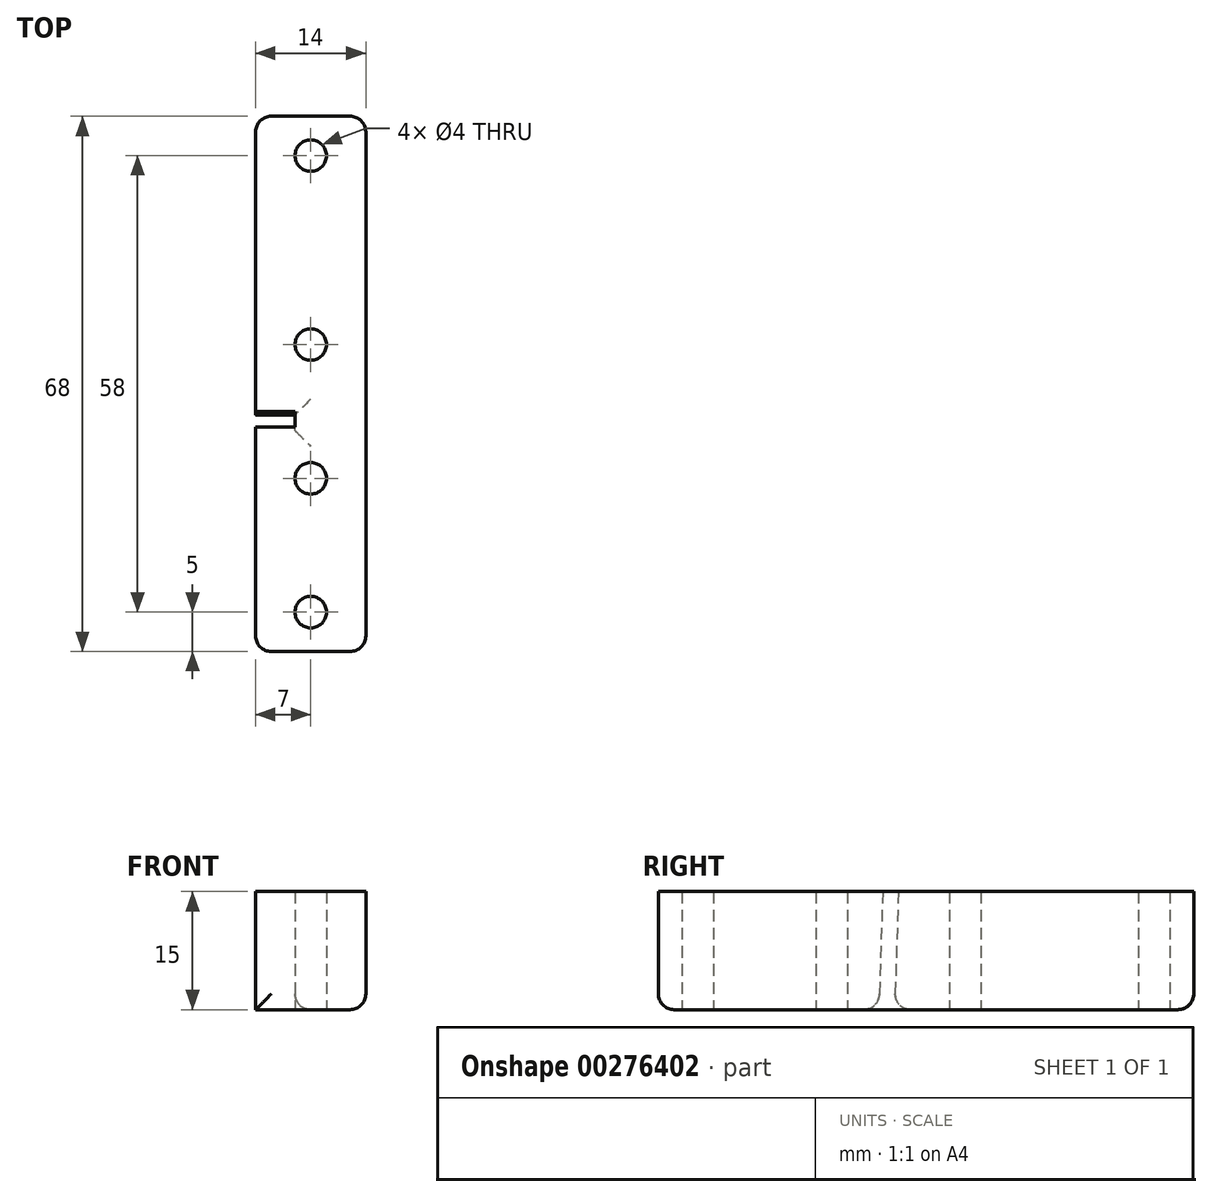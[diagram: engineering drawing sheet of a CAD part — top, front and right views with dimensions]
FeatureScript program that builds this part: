
annotation { "Feature Type Name" : "Feature", "Feature Type Description" : "" }
export const myFeature = defineFeature(function(context is Context, id is Id, definition is map)
    precondition{}
    {
        {
            var Q0;
            Q0=qCreatedBy(makeId("Top.planeOp"),FACE);
            var sketch = newSketch(context, id + "F0", { "sketchPlane" : qUnion([Q0])});
            skLineSegment(sketch, "E0.bottom", {"start": v(0, 0) * mm, "end": v(14, 0) * mm});
            skLineSegment(sketch, "E0.top", {"start": v(0, 68) * mm, "end": v(14, 68) * mm});
            skLineSegment(sketch, "E0.left", {"start": v(0, 0) * mm, "end": v(0, 28) * mm});
            skLineSegment(sketch, "E0.right", {"start": v(14, 0) * mm, "end": v(14, 28) * mm});
            skCircle(sketch, "E1", {"center": v(7, 5) * mm, "radius": 2 * mm});
            skPoint(sketch, "E1.centerSnap0", {"position": v(7, 0) * mm});
            skCircle(sketch, "E2", {"center": v(7, 22) * mm, "radius": 2 * mm});
            skLineSegment(sketch, "E3.bottom", {"start": v(0, 30) * mm, "end": v(14, 30) * mm});
            skLineSegment(sketch, "E3.top", {"start": v(0, 28) * mm, "end": v(14, 28) * mm});
            skLineSegment(sketch, "E4.trimOffspring", {"start": v(0, 30) * mm, "end": v(0, 68) * mm});
            skCircle(sketch, "E5", {"center": v(7, 39) * mm, "radius": 2 * mm});
            skLineSegment(sketch, "E6.trimOffspring", {"start": v(14, 30) * mm, "end": v(14, 68) * mm});
            skCircle(sketch, "E7", {"center": v(7, 63) * mm, "radius": 2 * mm});
            skSolve(sketch);
        }
        {
            var Q0;
            Q0=qSketchRegion(id+"F0",true);
            extrude(context, id + "F1", {"entities" : qUnion([Q0]), "offsetDistance" : 25 * mm, "depth" : 15 * mm});
        }
        {
            var Q0;
            Q0=makeQuery(id+"F1.opExtrude","SWEPT_FACE",FACE,{"disambiguationData":[OSD([sQuery(id+"F0.wireOp",EDGE,"E0.right")])]});
            var sketch = newSketch(context, id + "F2", { "sketchPlane" : qUnion([Q0])});
            skLineSegment(sketch, "E8.bottom", {"start": v(28, 15) * mm, "end": v(30.63, 15) * mm});
            skLineSegment(sketch, "E8.top", {"start": v(28, 0) * mm, "end": v(30.63, 0) * mm});
            skLineSegment(sketch, "E8.left", {"start": v(28, 15) * mm, "end": v(28, 0) * mm});
            skLineSegment(sketch, "E8.right", {"start": v(30.63, 15) * mm, "end": v(30.63, 0) * mm});
            skSolve(sketch);
        }
        {
            var Q0;
            Q0 = qSketchRegion(id + "F2", true);
            extrude(context, id + "F3", {"entities" : qUnion([Q0]), "operationType" : NewBodyOperationType.ADD, "oppositeDirection" : true, "depth" : 9 * mm, "offsetDistance" : 25 * mm});
        }
        {
            var Q0;
            Q0=makeQuery(id+"F1.opExtrude","SWEPT_FACE",FACE,{"disambiguationData":[OSD([sQuery(id+"F0.wireOp",EDGE,"E0.left")])]});
            var sketch = newSketch(context, id + "F4", { "sketchPlane" : qUnion([Q0])});
            skLineSegment(sketch, "E9", {"start": v(-28, 15) * mm, "end": v(-28.5, 15) * mm});
            skLineSegment(sketch, "E10", {"start": v(-28.5, 15) * mm, "end": v(-28, 0) * mm});
            skLineSegment(sketch, "E11", {"start": v(-28, 0) * mm, "end": v(-28, 15) * mm});
            skSolve(sketch);
        }
        {
            var Q0;
            Q0 = qSketchRegion(id + "F4", true);
            extrude(context, id + "F5", {"entities" : qUnion([Q0]), "operationType" : NewBodyOperationType.ADD, "oppositeDirection" : true, "depth" : 5 * mm, "offsetDistance" : 25 * mm});
        }
        {
            var Q0;
            Q0=makeQuery(id+"F1.opExtrude","SWEPT_FACE",FACE,{"disambiguationData":[OSD([sQuery(id+"F0.wireOp",EDGE,"E4.trimOffspring")])]});
            var sketch = newSketch(context, id + "F6", { "sketchPlane" : qUnion([Q0])});
            skLineSegment(sketch, "E12", {"start": v(-30, 15) * mm, "end": v(-30.5, 15) * mm});
            skLineSegment(sketch, "E13", {"start": v(-30.5, 15) * mm, "end": v(-30, 0) * mm});
            skLineSegment(sketch, "E14", {"start": v(-30, 0) * mm, "end": v(-30, 15) * mm});
            skSolve(sketch);
        }
        {
            var Q0;
            Q0 = qSketchRegion(id + "F6", true);
            extrude(context, id + "F7", {"entities" : qUnion([Q0]), "operationType" : NewBodyOperationType.REMOVE, "oppositeDirection" : true, "depth" : 5 * mm, "offsetDistance" : 25 * mm});
        }
        {
            var Q0;
            Q0=makeQuery(id+"F7.boolean.opBoolean","MERGE",EDGE,{"derivedFrom":[makeQuery(id+"F1.opExtrude","CAP_EDGE",EDGE,{"disambiguationData":[OSD([sQuery(id+"F0.wireOp",EDGE,"E3.bottom")])],"isStart":true}),makeQuery(id+"F7.opExtrude","SWEPT_EDGE",EDGE,{"disambiguationData":[OSD([sQuery(id+"F0.wireOp",EDGE,"E4.trimOffspring"),sQuery(id+"F6.wireOp",EDGE,"E13"),sQuery(id+"F6.wireOp",EDGE,"E14")])]})]});
            var Q1;
            Q1=makeQuery(id+"F3.opExtrude","CAP_EDGE",EDGE,{"disambiguationData":[OSD([sQuery(id+"F2.wireOp",EDGE,"E8.top")])],"isStart":false});
            var Q2;
            Q2=makeQuery(id+"F5.boolean.opBoolean","MERGE",EDGE,{"derivedFrom":[makeQuery(id+"F1.opExtrude","CAP_EDGE",EDGE,{"disambiguationData":[OSD([sQuery(id+"F0.wireOp",EDGE,"E3.top")])],"isStart":true}),makeQuery(id+"F5.opExtrude","SWEPT_EDGE",EDGE,{"disambiguationData":[OSD([sQuery(id+"F0.wireOp",EDGE,"E0.left"),sQuery(id+"F4.wireOp",EDGE,"E10"),sQuery(id+"F4.wireOp",EDGE,"E11")])]})]});
            var Q3;
            Q3=makeQuery(id+"F1.opExtrude","CAP_EDGE",EDGE,{"disambiguationData":[OSD([sQuery(id+"F0.wireOp",EDGE,"E0.bottom")])],"isStart":true});
            var Q4;
            Q4=makeQuery(id+"F3.boolean.opBoolean","MERGE",EDGE,{"derivedFrom":[makeQuery(id+"F1.opExtrude","CAP_EDGE",EDGE,{"disambiguationData":[OSD([sQuery(id+"F0.wireOp",EDGE,"E0.right")])],"isStart":true}),makeQuery(id+"F1.opExtrude","CAP_EDGE",EDGE,{"disambiguationData":[OSD([sQuery(id+"F0.wireOp",EDGE,"E6.trimOffspring")])],"isStart":true}),makeQuery(id+"F3.opExtrude","CAP_EDGE",EDGE,{"disambiguationData":[OSD([sQuery(id+"F2.wireOp",EDGE,"E8.top")])],"isStart":true})]});
            var Q5;
            Q5=makeQuery(id+"F1.opExtrude","CAP_EDGE",EDGE,{"disambiguationData":[OSD([sQuery(id+"F0.wireOp",EDGE,"E0.top")])],"isStart":true});
            var Q6;
            Q6=makeQuery(id+"F1.opExtrude","SWEPT_EDGE",EDGE,{"disambiguationData":[OSD([sQuery(id+"F0.wireOp",EDGE,"E0.top"),sQuery(id+"F0.wireOp",EDGE,"E4.trimOffspring")])]});
            var Q7;
            Q7=makeQuery(id+"F1.opExtrude","SWEPT_EDGE",EDGE,{"disambiguationData":[OSD([sQuery(id+"F0.wireOp",EDGE,"E0.top"),sQuery(id+"F0.wireOp",EDGE,"E6.trimOffspring")])]});
            var Q8;
            Q8=makeQuery(id+"F1.opExtrude","SWEPT_EDGE",EDGE,{"disambiguationData":[OSD([sQuery(id+"F0.wireOp",EDGE,"E0.bottom"),sQuery(id+"F0.wireOp",EDGE,"E0.left")])]});
            var Q9;
            Q9=makeQuery(id+"F1.opExtrude","SWEPT_EDGE",EDGE,{"disambiguationData":[OSD([sQuery(id+"F0.wireOp",EDGE,"E0.bottom"),sQuery(id+"F0.wireOp",EDGE,"E0.right")])]});
            fillet(context, id + "F8", {"entities" : qUnion([Q0, Q1, Q2, Q3, Q4, Q5, Q6, Q7, Q8, Q9]), "radius" : 2 * mm, "tangentPropagation" : true, "defaultsChanged" : false, "vertexSettings" : [], "allowEdgeOverflow" : false});
        }
    });
